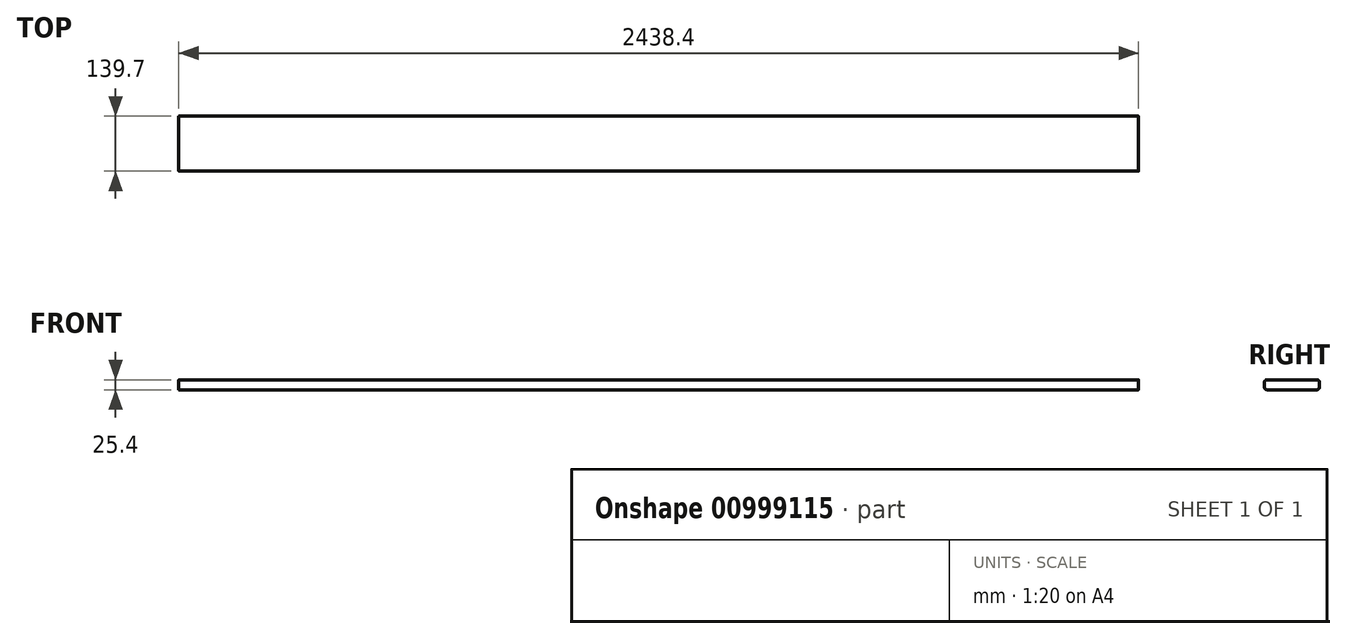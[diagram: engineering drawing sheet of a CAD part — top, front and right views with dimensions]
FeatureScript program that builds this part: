
annotation { "Feature Type Name" : "Feature", "Feature Type Description" : "" }
export const myFeature = defineFeature(function(context is Context, id is Id, definition is map)
    precondition{}
    {
        {
            var Q0;
            Q0=qCreatedBy(makeId("Top.planeOp"),FACE);
            var sketch = newSketch(context, id + "F0", { "sketchPlane" : qUnion([Q0])});
            skLineSegment(sketch, "E0.bottom", {"start": v(-1219.2, 0) * mm, "end": v(1219.2, 0) * mm});
            skLineSegment(sketch, "E0.top", {"start": v(-1219.2, -139.7) * mm, "end": v(1219.2, -139.7) * mm});
            skLineSegment(sketch, "E0.left", {"start": v(-1219.2, 0) * mm, "end": v(-1219.2, -139.7) * mm});
            skLineSegment(sketch, "E0.right", {"start": v(1219.2, 0) * mm, "end": v(1219.2, -139.7) * mm});
            skSolve(sketch);
        }
        {
            var Q0;
            Q0 = qSketchRegion(id + "F0", true);
            extrude(context, id + "F1", {"entities" : qUnion([Q0]), "depth" : 25.4 * mm, "offsetDistance" : 25.4 * mm});
        }
        {
            var Q0;
            Q0=makeQuery(id+"F1.opExtrude","CAP_EDGE",EDGE,{"disambiguationData":[OSD([sQuery(id+"F0.wireOp",EDGE,"E0.bottom")])],"isStart":false});
            var Q1;
            Q1=makeQuery(id+"F1.opExtrude","CAP_EDGE",EDGE,{"disambiguationData":[OSD([sQuery(id+"F0.wireOp",EDGE,"E0.top")])],"isStart":false});
            var Q2;
            Q2=makeQuery(id+"F1.opExtrude","CAP_EDGE",EDGE,{"disambiguationData":[OSD([sQuery(id+"F0.wireOp",EDGE,"E0.top")])],"isStart":true});
            var Q3;
            Q3=makeQuery(id+"F1.opExtrude","CAP_EDGE",EDGE,{"disambiguationData":[OSD([sQuery(id+"F0.wireOp",EDGE,"E0.bottom")])],"isStart":true});
            fillet(context, id + "F2", {"entities" : qUnion([Q0, Q1, Q2, Q3]), "tangentPropagation" : true, "radius" : 6.35 * mm, "defaultsChanged" : false, "vertexSettings" : [], "allowEdgeOverflow" : false});
        }
    });
